# Revit family: FP-Revit18-en-DD24DTX6PX1-DishDrawer-0-US-CA-90002261A
name_source: partatom
category: Specialty Equipment
revit_build: Autodesk Revit 2018 (Build: 20170223_1515(x64)
units: mm (PartAtom-declared; Revit-internal decimal feet)

## family parameters
Always vertical = Yes
Cut with Voids When Loaded = Yes
OmniClass Number = 23.40.40.14.31
OmniClass Title = Cleaning and Disposal Equipment
Part Type = Normal
Room Calculation Point = No
Round Connector Dimension = Use Diameter
Shared = No
Work Plane-Based = No

## types (1)
- DD24DTX6X1
    Cavity - Depth = 578 mm  [stored 1.89633 ft]
    Cavity - Height = 0 mm  [stored 0 ft]
    Cavity - Width = 600 mm  [stored 1.9685 ft]
    Chassis - Height = 856 mm  [stored 2.8084 ft]
    Connector Description - Electrical = 110-120 V, 15 A, fused electrical supply
    Connector Description - Sanitary = Drain Hose, No Fitting Required
    Connector Description - Water = Supplied hose to suit 3⁄8” (9 mm) male compression fitting
    Description = Double DishDrawer™ Dishwasher, Tall
    Manufacturer = Fisher & Paykel Appliances
    Material - Body = Fisher & Paykel - Grey
    Material - Buttons and Dials = Fisher & Paykel - Aluminium
    Material - Door Front = Fisher & Paykel - Stainless Steel
    Material - Toe Kick = Fisher & Paykel - Black
    Material - Trim = Fisher & Paykel - Aluminium
    Model = DD24DTX6X1
    Product - Depth = 573 mm  [stored 1.87992 ft]
    Product - Width = 599 mm  [stored 1.96522 ft]
    URL = www.fisherpaykel.com
    Visibility - Clearance Required = Yes

note: [stored X ft] marks values corroborated as IEEE doubles in the binary element streams (Revit-internal decimal feet)

## geometry (parser evidence)
native form markers: Sweep x5
no freeform markers — native parametric forms only
